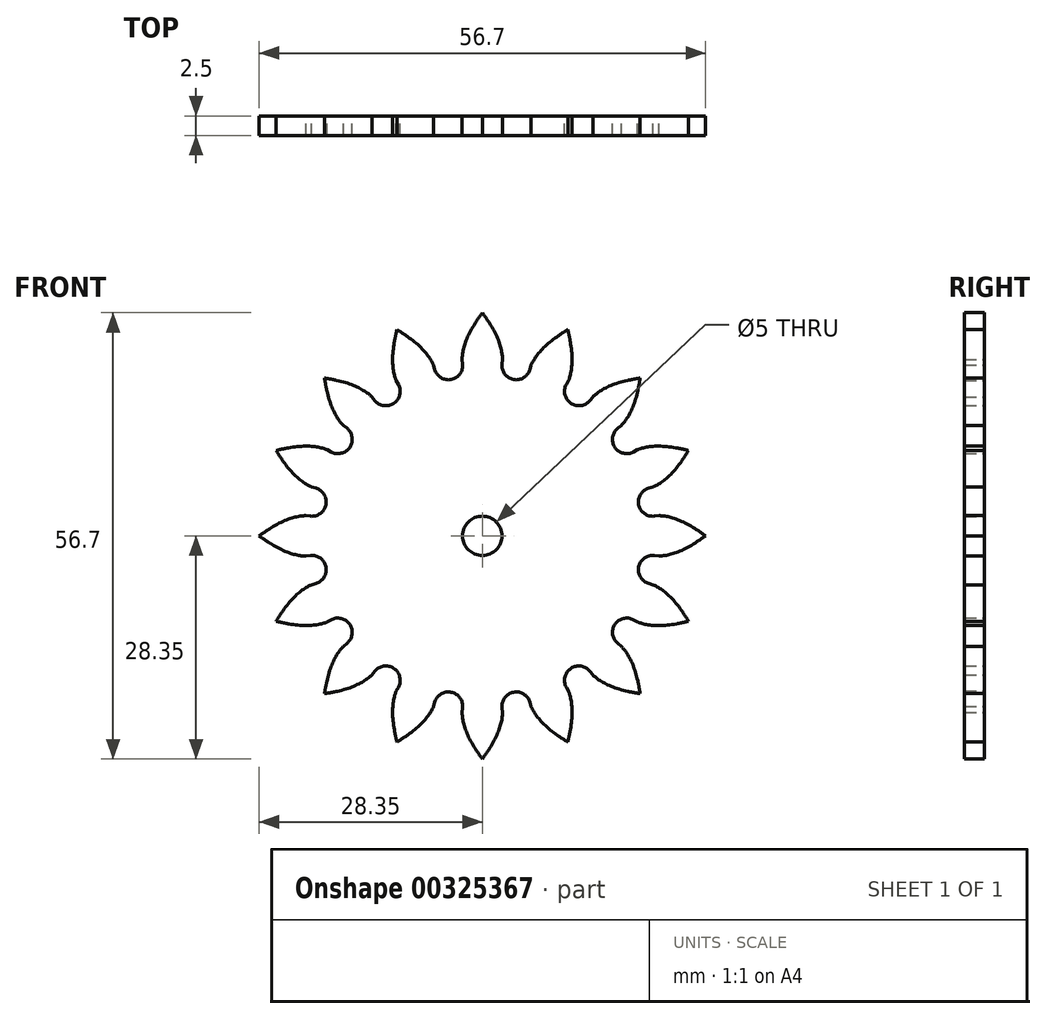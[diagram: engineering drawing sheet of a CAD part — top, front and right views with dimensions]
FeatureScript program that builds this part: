
annotation { "Feature Type Name" : "Feature", "Feature Type Description" : "" }
export const myFeature = defineFeature(function(context is Context, id is Id, definition is map)
    precondition{}
    {
        {
            assignVariable(context, id + "F0", {"name" : "NumberOfTeeth", "anyValue" : 16});
        }
        {
            var Q0;
            Q0=qCreatedBy(makeId("Front.planeOp"),FACE);
            var sketch = newSketch(context, id + "F1", { "sketchPlane" : qUnion([Q0])});
            skCircle(sketch, "E0", {"center": v(0, 0) * mm, "radius": 20.25 * mm});
            skSolve(sketch);
        }
        {
            var Q0;
            Q0=qSketchRegion(id+"F1",true);
            extrude(context, id + "F2", {"entities" : qUnion([Q0]), "depth" : 2.5 * mm});
        }
        {
            var Q0;
            Q0=qCreatedBy(makeId("Front.planeOp"),FACE);
            var sketch = newSketch(context, id + "F3", { "sketchPlane" : qUnion([Q0])});
            skCircle(sketch, "E1", {"center": v(0, 0) * mm, "radius": 24 * mm, "construction": true});
            skLineSegment(sketch, "E2", {"start": v(0, 0) * mm, "end": v(2.35, 23.88) * mm, "construction": true});
            skCircle(sketch, "E3.0", {"center": v(0, 0) * mm, "radius": 20.25 * mm, "construction": true});
            skLineSegment(sketch, "E4", {"start": v(0, 0) * mm, "end": v(4.68, 23.54) * mm, "construction": true});
            skCircle(sketch, "E5", {"center": v(0, 0) * mm, "radius": 22.55 * mm, "construction": true});
            skLineSegment(sketch, "E6", {"start": v(0, 0) * mm, "end": v(2.56, 22.4) * mm, "construction": true});
            skLineSegment(sketch, "E7", {"start": v(0, 0) * mm, "end": v(-3.44, 22.29) * mm, "construction": true});
            skLineSegment(sketch, "E8", {"start": v(0, 0) * mm, "end": v(-9.2, 20.6) * mm, "construction": true});
            skLineSegment(sketch, "E9", {"start": v(0, 0) * mm, "end": v(-14.3, 17.44) * mm, "construction": true});
            skLineSegment(sketch, "E10", {"start": v(0, 0) * mm, "end": v(-18.39, 13.06) * mm, "construction": true});
            skLineSegment(sketch, "E11", {"start": v(2.56, 22.4) * mm, "end": v(-3.44, 22.29) * mm, "construction": true});
            skLineSegment(sketch, "E12", {"start": v(-3.44, 22.29) * mm, "end": v(-9.2, 20.6) * mm, "construction": true});
            skLineSegment(sketch, "E13", {"start": v(-9.2, 20.6) * mm, "end": v(-14.3, 17.44) * mm, "construction": true});
            skLineSegment(sketch, "E14", {"start": v(-14.3, 17.44) * mm, "end": v(-18.39, 13.06) * mm, "construction": true});
            skLineSegment(sketch, "E15", {"start": v(0, 0) * mm, "end": v(-21.18, 7.74) * mm, "construction": true});
            skLineSegment(sketch, "E16", {"start": v(-18.39, 13.06) * mm, "end": v(-21.18, 7.74) * mm, "construction": true});
            skLineSegment(sketch, "E17", {"start": v(-3.44, 22.29) * mm, "end": v(2.5, 23.2) * mm, "construction": true});
            skLineSegment(sketch, "E18", {"start": v(-9.2, 20.6) * mm, "end": v(1.77, 25.49) * mm, "construction": true});
            skLineSegment(sketch, "E19", {"start": v(-14.3, 17.44) * mm, "end": v(-0.37, 28.85) * mm, "construction": true});
            skLineSegment(sketch, "E20", {"start": v(-18.39, 13.06) * mm, "end": v(-4.5, 32.63) * mm, "construction": true});
            skLineSegment(sketch, "E21", {"start": v(-21.18, 7.74) * mm, "end": v(-10.88, 35.92) * mm, "construction": true});
            skLineSegment(sketch, "E22", {"start": v(2.56, 22.4) * mm, "end": v(2.5, 21.85) * mm});
            skArc(sketch, "E23", {"start": v(2.5, 21.85) * mm, "mid": v(2.84, 20.57) * mm, "end": v(3.95, 19.86) * mm});
            skLineSegment(sketch, "E24", {"start": v(3.95, 19.86) * mm, "end": v(0, 0) * mm});
            skCircle(sketch, "E25", {"center": v(0, 0) * mm, "radius": 27 * mm, "construction": true});
            skFitSpline(sketch, "E26", {"points": [v(2.56, 22.4) * mm, v(2.5, 23.2) * mm, v(1.77, 25.49) * mm, v(-0.37, 28.85) * mm, v(-4.5, 32.63) * mm, v(-10.88, 35.92) * mm], "startDerivative": vector(0.12, 3.06) * mm, "endDerivative": vector(-7.31, 8.58) * mm});
            skFitSpline(sketch, "E27.MirrorCS", {"points": [v(-2.56, 22.4) * mm, v(-2.5, 23.2) * mm, v(-1.77, 25.49) * mm, v(0.37, 28.85) * mm, v(4.5, 32.63) * mm, v(10.88, 35.92) * mm], "startDerivative": vector(-0.12, 3.06) * mm, "endDerivative": vector(7.31, 8.58) * mm});
            skLineSegment(sketch, "E28.MirrorCS", {"start": v(-2.56, 22.4) * mm, "end": v(-2.5, 21.85) * mm});
            skArc(sketch, "E29.MirrorCS", {"start": v(-2.5, 21.85) * mm, "mid": v(-2.84, 20.57) * mm, "end": v(-3.95, 19.86) * mm});
            skLineSegment(sketch, "E30", {"start": v(-0.93, 26.98) * mm, "end": v(0.9, 27.05) * mm});
            skFitSpline(sketch, "E31.trimOffspring", {"points": [v(2.56, 22.4) * mm, v(2.5, 23.2) * mm, v(1.77, 25.49) * mm, v(-0.37, 28.85) * mm, v(-4.5, 32.63) * mm, v(-10.88, 35.92) * mm], "startDerivative": vector(0.12, 3.06) * mm, "endDerivative": vector(-7.31, 8.58) * mm});
            skFitSpline(sketch, "E32.trimOffspring", {"points": [v(-2.56, 22.4) * mm, v(-2.5, 23.2) * mm, v(-1.77, 25.49) * mm, v(0.37, 28.85) * mm, v(4.5, 32.63) * mm, v(10.88, 35.92) * mm], "startDerivative": vector(-0.12, 3.06) * mm, "endDerivative": vector(7.31, 8.58) * mm});
            skLineSegment(sketch, "E33", {"start": v(-3.95, 19.86) * mm, "end": v(0, 0) * mm});
            skSolve(sketch);
        }
        {
            var Q0;
            Q0=qSketchRegion(id+"F3",true);
            extrude(context, id + "F4", {"entities" : qUnion([Q0]), "depth" : 2.5 * mm});
        }
        {
            var Q0;
            Q0=makeQuery(id+"F4.opExtrude","SWEPT_BODY",BODY,{"disambiguationData":[OSD([sQuery(id+"F3.wireOp",EDGE,"E22"),sQuery(id+"F3.wireOp",EDGE,"E23"),sQuery(id+"F3.wireOp",EDGE,"E24"),sQuery(id+"F3.wireOp",EDGE,"02dd0c5d-d1e8-4f79-863c-406f84435db1"),sQuery(id+"F3.wireOp",EDGE,"m1XDvlc8-NUZd-qkRk-q4Va-xkGgnuwNPfDB"),sQuery(id+"F3.wireOp",EDGE,"fcaf4da5-0803-456f-80d9-8ebba38615120.MirrorCS"),sQuery(id+"F3.wireOp",EDGE,"aedb47dc-a047-4e1f-8bb6-d5fbd5fdca930.MirrorCS"),sQuery(id+"F3.wireOp",EDGE,"a5371087-b1d2-494e-a018-3e77599f56c10.MirrorCS"),sQuery(id+"F3.wireOp",EDGE,"c3ac059d-0bc8-484a-9e2b-dc5b0a2fc6190.MirrorCS"),sQuery(id+"F3.wireOp",EDGE,"7677bc88-b94f-4734-94cb-964bed4e21a90.MirrorCS")])]});
            var Q1;
            Q1=sQuery(id+"F1.wireOp",EDGE,"E0");
            circularPattern(context, id + "F5", {"operationType" : NewBodyOperationType.ADD, "entities" : qUnion([Q0]), "axis" : qUnion([Q1]), "angle" : 360 * degree, "instanceCount" : getVariable(context, 'NumberOfTeeth'), "equalSpace" : true});
        }
        {
            var Q0;
            {var subQ0=makeQuery(id+"F4.opExtrude","CAP_FACE",FACE,{"disambiguationData":[OSD([sQuery(id+"F3.wireOp",EDGE,"1f885de5-3e7a-432a-b88a-3eaa30a7a401.0"),sQuery(id+"F3.wireOp",EDGE,"A7tLEwBN-HnOb-phWn-sB40-qaaEkIq7NDu9"),sQuery(id+"F3.wireOp",EDGE,"94f80f61-b426-4ec2-81a6-44f42ff73b0d"),sQuery(id+"F3.wireOp",EDGE,"3276b7df-17ce-42f5-8fef-bbce2681202d"),sQuery(id+"F3.wireOp",EDGE,"8cab6697-fc05-46dd-9d4d-494c43dbe1bc"),sQuery(id+"F3.wireOp",EDGE,"267e9553-86ea-40c7-a68d-067ff4e522c80.MirrorCS"),sQuery(id+"F3.wireOp",EDGE,"0081c8b5-e93b-4ec3-87cf-ae34b8c9de0e0.MirrorCS"),sQuery(id+"F3.wireOp",EDGE,"14eaaf62-2f47-4f70-a4e9-6a61db97f38f0.MirrorCS"),sQuery(id+"F3.wireOp",EDGE,"36c0f882-098c-494c-bc9e-4a3fa39534f60.MirrorCS")])],"isStart":false});Q0=makeQuery(id+"F5.boolean.opBoolean","MERGE",FACE,{"derivedFrom":[makeQuery(id+"F2.opExtrude","CAP_FACE",FACE,{"disambiguationData":[OSD([sQuery(id+"F1.wireOp",EDGE,"E0")])],"isStart":false}),subQ0,makeQuery(id+"F5.opPattern","COPY",FACE,{"derivedFrom":subQ0,"instanceName":"1"}),makeQuery(id+"F5.opPattern","COPY",FACE,{"derivedFrom":subQ0,"instanceName":"2"}),makeQuery(id+"F5.opPattern","COPY",FACE,{"derivedFrom":subQ0,"instanceName":"3"}),makeQuery(id+"F5.opPattern","COPY",FACE,{"derivedFrom":subQ0,"instanceName":"4"}),makeQuery(id+"F5.opPattern","COPY",FACE,{"derivedFrom":subQ0,"instanceName":"5"}),makeQuery(id+"F5.opPattern","COPY",FACE,{"derivedFrom":subQ0,"instanceName":"6"}),makeQuery(id+"F5.opPattern","COPY",FACE,{"derivedFrom":subQ0,"instanceName":"7"}),makeQuery(id+"F5.opPattern","COPY",FACE,{"derivedFrom":subQ0,"instanceName":"8"}),makeQuery(id+"F5.opPattern","COPY",FACE,{"derivedFrom":subQ0,"instanceName":"9"}),makeQuery(id+"F5.opPattern","COPY",FACE,{"derivedFrom":subQ0,"instanceName":"10"}),makeQuery(id+"F5.opPattern","COPY",FACE,{"derivedFrom":subQ0,"instanceName":"11"}),makeQuery(id+"F5.opPattern","COPY",FACE,{"derivedFrom":subQ0,"instanceName":"12"}),makeQuery(id+"F5.opPattern","COPY",FACE,{"derivedFrom":subQ0,"instanceName":"13"}),makeQuery(id+"F5.opPattern","COPY",FACE,{"derivedFrom":subQ0,"instanceName":"14"}),makeQuery(id+"F5.opPattern","COPY",FACE,{"derivedFrom":subQ0,"instanceName":"15"}),makeQuery(id+"F5.opPattern","COPY",FACE,{"derivedFrom":subQ0,"instanceName":"16"}),makeQuery(id+"F5.opPattern","COPY",FACE,{"derivedFrom":subQ0,"instanceName":"17"}),makeQuery(id+"F5.opPattern","COPY",FACE,{"derivedFrom":subQ0,"instanceName":"18"}),makeQuery(id+"F5.opPattern","COPY",FACE,{"derivedFrom":subQ0,"instanceName":"19"})]});}
            var sketch = newSketch(context, id + "F6", { "sketchPlane" : qUnion([Q0])});
            skCircle(sketch, "E34", {"center": v(0, 0) * mm, "radius": 2.5 * mm});
            skSolve(sketch);
        }
        {
            var Q0;
            Q0=qSketchRegion(id+"F6",true);
            extrude(context, id + "F7", {"entities" : qUnion([Q0]), "operationType" : NewBodyOperationType.REMOVE, "endBound" : BoundingType.THROUGH_ALL, "oppositeDirection" : true, "depth" : 25 * mm});
        }
    });
